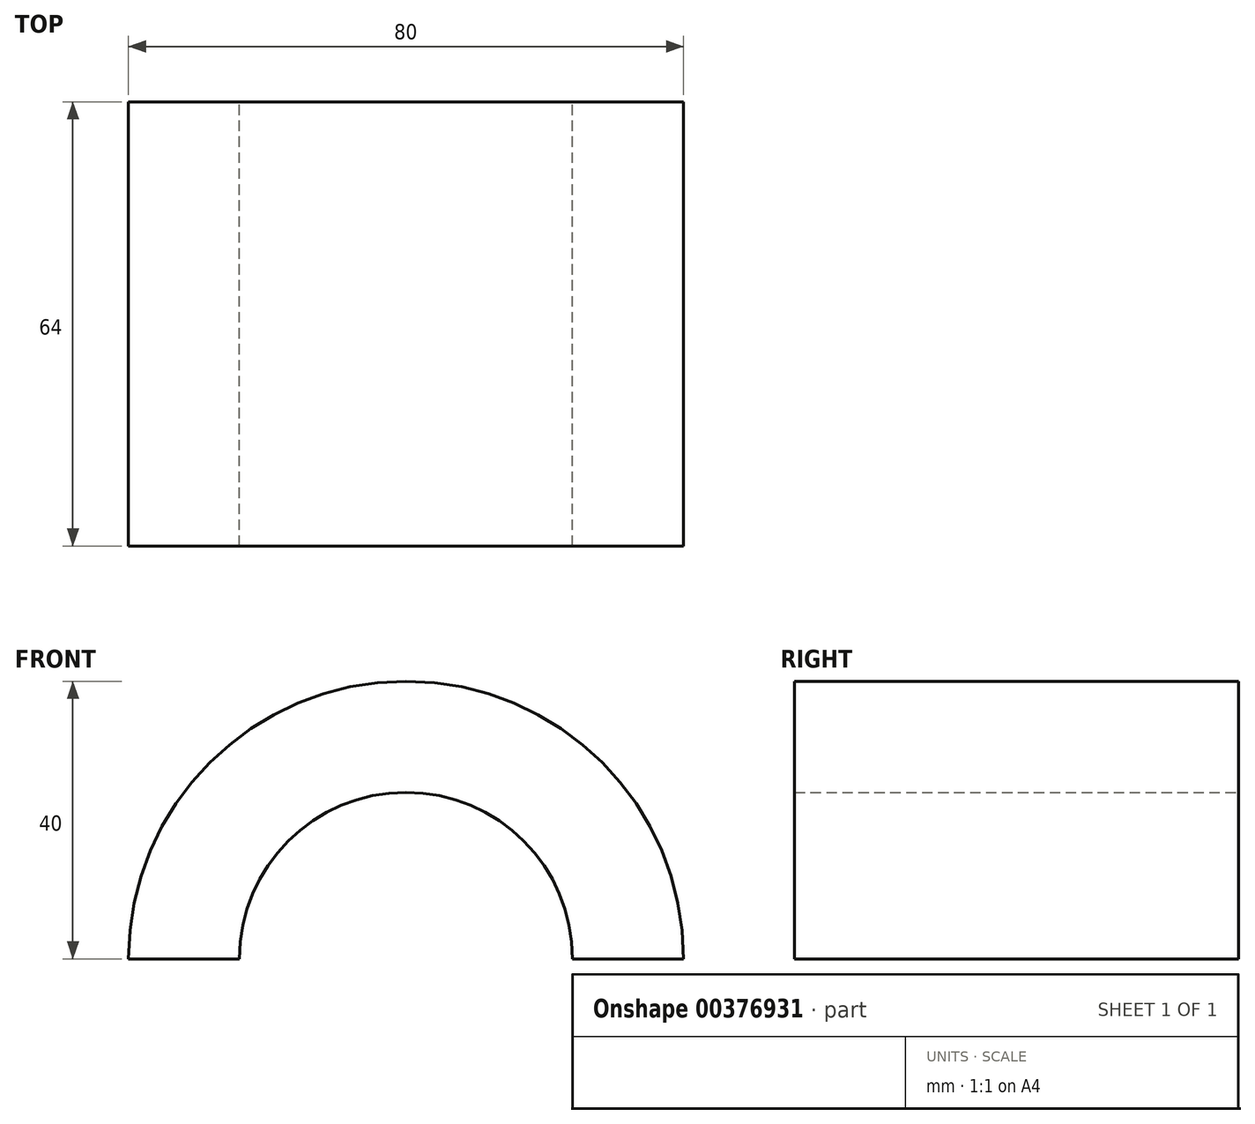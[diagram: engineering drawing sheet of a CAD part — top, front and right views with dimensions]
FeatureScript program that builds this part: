
annotation { "Feature Type Name" : "Feature", "Feature Type Description" : "" }
export const myFeature = defineFeature(function(context is Context, id is Id, definition is map)
    precondition{}
    {
        {
            var Q0;
            Q0=qCreatedBy(makeId("Front.planeOp"),FACE);
            var sketch = newSketch(context, id + "F0", { "sketchPlane" : qUnion([Q0])});
            skArc(sketch, "E0", {"start": v(24, 0) * mm, "mid": v(0, 24) * mm, "end": v(-24, 0) * mm});
            skArc(sketch, "E1", {"start": v(40, 0) * mm, "mid": v(0, 40) * mm, "end": v(-40, 0) * mm});
            skLineSegment(sketch, "E2", {"start": v(-24, 0) * mm, "end": v(24, 0) * mm, "construction": true});
            skPoint(sketch, "E3", {"position": v(24, 0) * mm});
            skLineSegment(sketch, "E4", {"start": v(-40, 0) * mm, "end": v(-24, 0) * mm});
            skLineSegment(sketch, "E5", {"start": v(24, 0) * mm, "end": v(40, 0) * mm});
            skSolve(sketch);
        }
        {
            var Q0;
            Q0=makeQuery(id+"F0.imprint","IMPRINT",FACE,{"disambiguationData":[TD([[makeQuery(id+"F0.imprint","IMPRINT",EDGE,{"derivedFrom":sQuery(id+"F0.wireOp",EDGE,"E0")}),-1.0]])]});
            extrude(context, id + "F1", {"entities" : qUnion([Q0]), "endBound" : BoundingType.SYMMETRIC, "depth" : 64 * mm});
        }
    });
